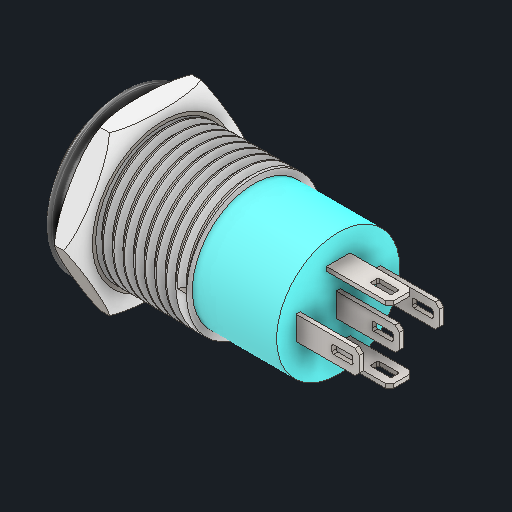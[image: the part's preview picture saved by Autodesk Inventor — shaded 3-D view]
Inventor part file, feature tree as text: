
AUTODESK INVENTOR PART (.ipt)
format: ipt  version: 2022 (Build 260153000, 153)  size: 488,448 bytes
history: mixed  units: in
note: dims shown in document units (in); Inventor stores cm internally (conversion verified against a paired STEP export)
features: revolve x1, other x1, imported_body x1
ambient origin geometry x8: Origin, YZ Plane, XZ Plane, XY Plane, X Axis, Y Axis, Z Axis, Center Point
bodies: Solid1 (imported_parasolid), Solid2 (imported_parasolid)
feature tree (3):
  revolve  "Revolve2"  [1 undecoded]
  other  "Cut-Extrude3"
  imported_body  NMx_Import_Brep_tag  [imported B-rep: ~10 faces, bbox_mm=[0.0, 0.0, 0.0]]
note: 1 required parameter value undecoded (feature->parameter linkage not recoverable at this tier; creation-order binding heuristic only, values carry confidence <= 0.55)
